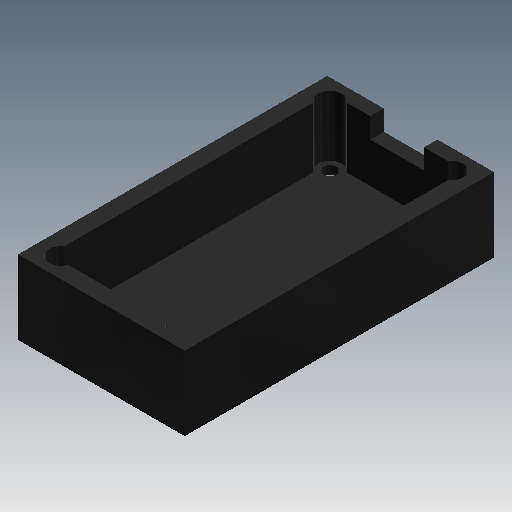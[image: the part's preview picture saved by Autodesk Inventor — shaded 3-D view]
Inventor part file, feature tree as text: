
AUTODESK INVENTOR PART (.ipt)
format: ipt  version: 2017 (Build 210142000, 142)  size: 147,968 bytes
history: native  units: mm
features: sketch x5, extrude x4, projected_geometry x2, other x1, hole x1
ambient origin geometry x8: Origin, YZ Plane, XZ Plane, XY Plane, X Axis, Y Axis, Z Axis, Center Point
bodies: Body1 (feature_tree)
feature tree (13):
  other  "Твердое тело1"
  extrude  "Выдавливание1"  Depth=12.4mm
  extrude  "Выдавливание2"  Depth=23.0mm
  hole  "Отверстие1"  [1 undecoded]
  extrude  "Выдавливание3"  Depth=1.0mm
  extrude  "Выдавливание4"  Depth=1.2mm
  sketch  "Эскиз1"
  sketch  "Эскиз2"
  projected_geometry  "Спроецированная петля1"
  sketch  "Эскиз3"
  sketch  "Эскиз4"
  sketch  "Эскиз5"
  projected_geometry  "Спроецированная петля2"
note: 1 required parameter value undecoded (feature->parameter linkage not recoverable at this tier; creation-order binding heuristic only, values carry confidence <= 0.55)
